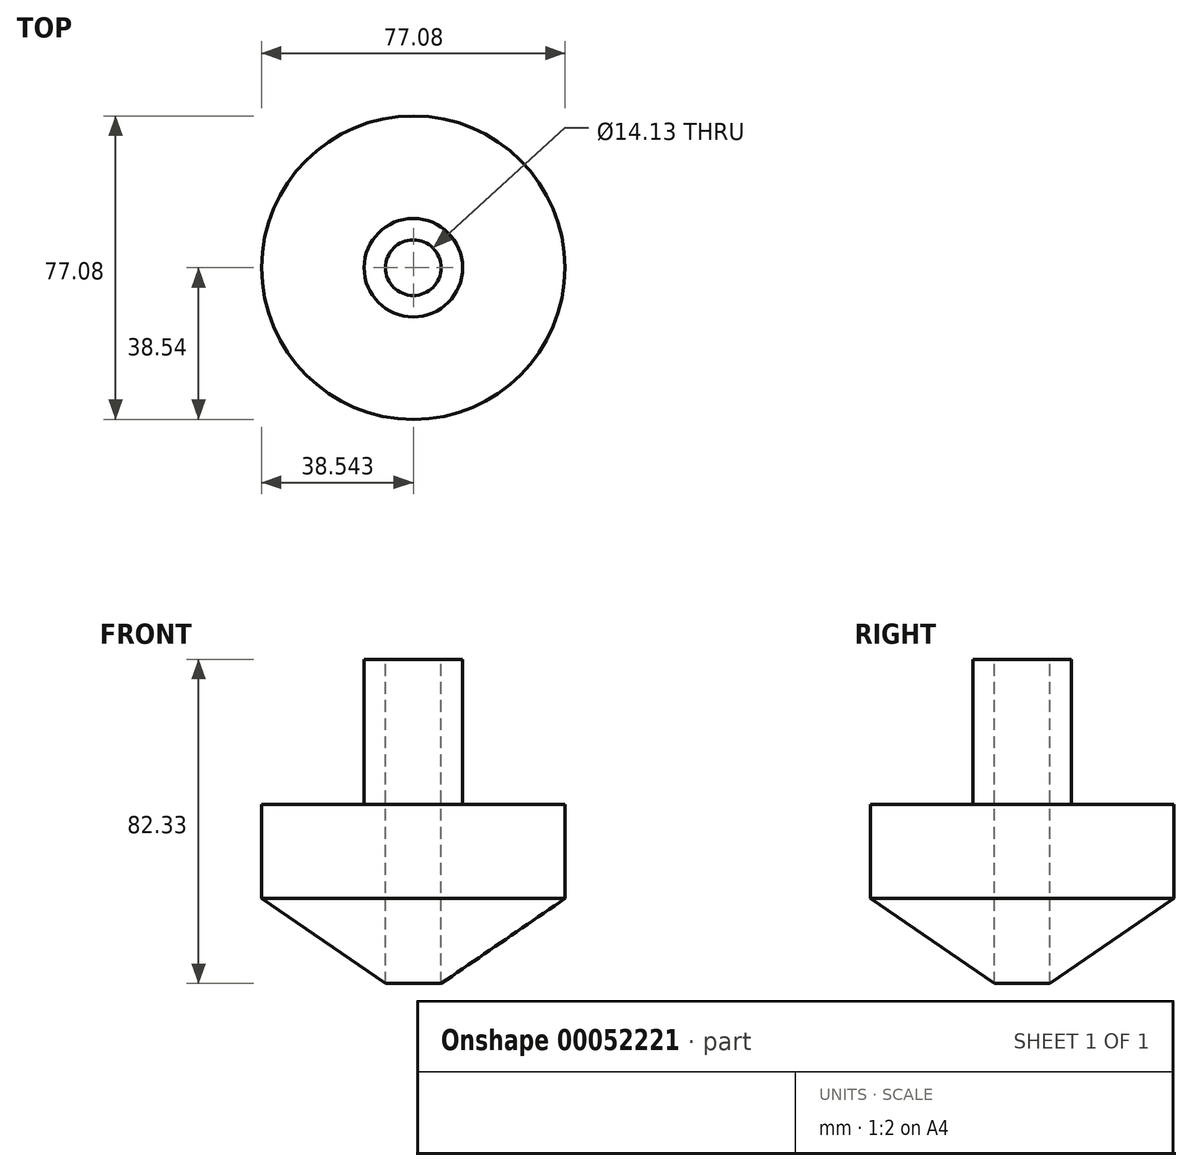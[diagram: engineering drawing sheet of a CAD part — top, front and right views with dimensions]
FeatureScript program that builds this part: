
annotation { "Feature Type Name" : "Feature", "Feature Type Description" : "" }
export const myFeature = defineFeature(function(context is Context, id is Id, definition is map)
    precondition{}
    {
        {
            var Q0;
            Q0=qCreatedBy(makeId("Front.planeOp"),FACE);
            var sketch = newSketch(context, id + "F0", { "sketchPlane" : qUnion([Q0])});
            skLineSegment(sketch, "E0", {"start": v(0, 36.83) * mm, "end": v(-5.45, 36.83) * mm});
            skLineSegment(sketch, "E1", {"start": v(-5.45, 36.83) * mm, "end": v(-5.45, 0) * mm});
            skLineSegment(sketch, "E2", {"start": v(-5.45, 0) * mm, "end": v(-31.48, 0) * mm});
            skLineSegment(sketch, "E3", {"start": v(-31.48, 0) * mm, "end": v(-31.48, -23.91) * mm});
            skLineSegment(sketch, "E4", {"start": v(-31.48, -23.91) * mm, "end": v(0, -45.5) * mm});
            skLineSegment(sketch, "E5", {"start": v(7.06, 36.83) * mm, "end": v(7.06, -45.5) * mm});
            skLineSegment(sketch, "E6", {"start": v(0, 36.83) * mm, "end": v(0, -45.5) * mm});
            skSolve(sketch);
        }
        {
            var Q0;
            Q0=makeQuery(id+"F0.imprint","IMPRINT",FACE,{"disambiguationData":[TD([[makeQuery(id+"F0.imprint","IMPRINT",EDGE,{"derivedFrom":sQuery(id+"F0.wireOp",EDGE,"E0")}),1.0]])]});
            var Q1;
            Q1=sQuery(id+"F0.wireOp",EDGE,"E5");
            revolve(context, id + "F1", {"entities" : qUnion([Q0]), "axis" : qUnion([Q1]), "revolveType" : RevolveType.FULL});
        }
    });
